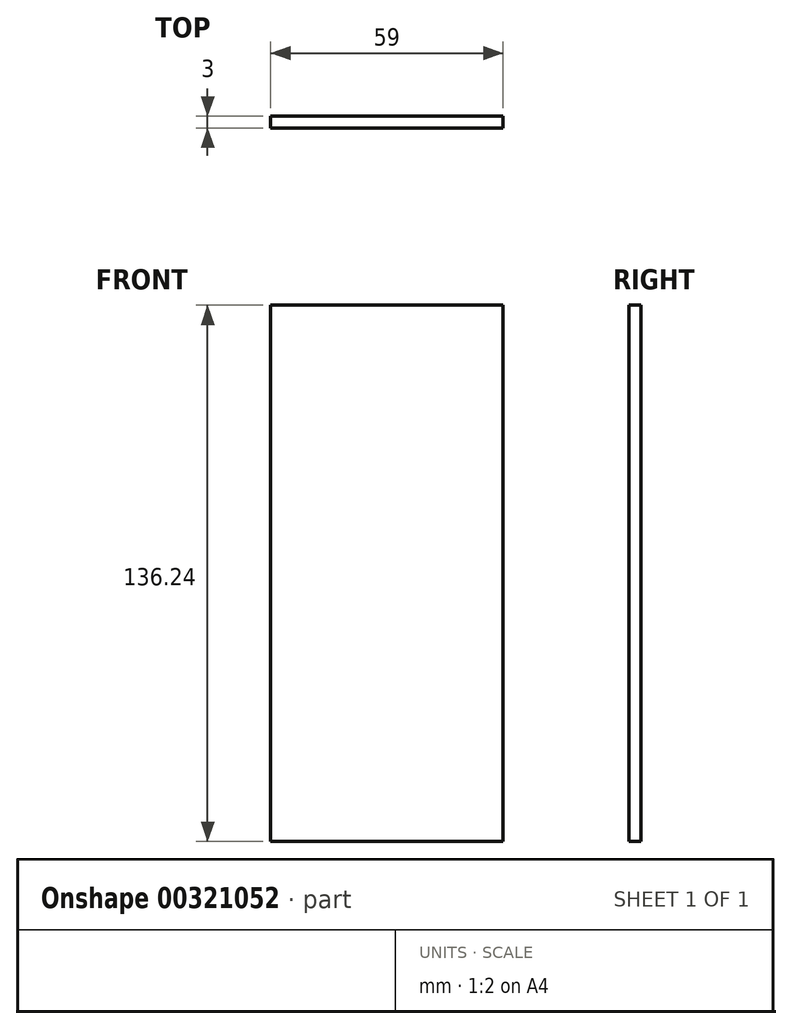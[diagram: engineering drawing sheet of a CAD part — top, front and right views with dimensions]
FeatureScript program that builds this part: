
annotation { "Feature Type Name" : "Feature", "Feature Type Description" : "" }
export const myFeature = defineFeature(function(context is Context, id is Id, definition is map)
    precondition{}
    {
        {
            var Q0;
            Q0=qCreatedBy(makeId("Front.planeOp"),FACE);
            var sketch = newSketch(context, id + "F0", { "sketchPlane" : qUnion([Q0])});
            skLineSegment(sketch, "E0.bottom", {"start": v(29.5, 68.12) * mm, "end": v(-29.5, 68.12) * mm});
            skLineSegment(sketch, "E0.top", {"start": v(29.5, -68.13) * mm, "end": v(-29.5, -68.13) * mm});
            skLineSegment(sketch, "E0.left", {"start": v(29.5, 68.12) * mm, "end": v(29.5, -68.13) * mm});
            skLineSegment(sketch, "E0.right", {"start": v(-29.5, 68.12) * mm, "end": v(-29.5, -68.13) * mm});
            skPoint(sketch, "E0.middle", {"position": v(0, 0) * mm});
            skSolve(sketch);
        }
        {
            var Q0;
            Q0 = qSketchRegion(id + "F0", true);
            extrude(context, id + "F1", {"entities" : qUnion([Q0]), "depth" : 3 * mm});
        }
    });
